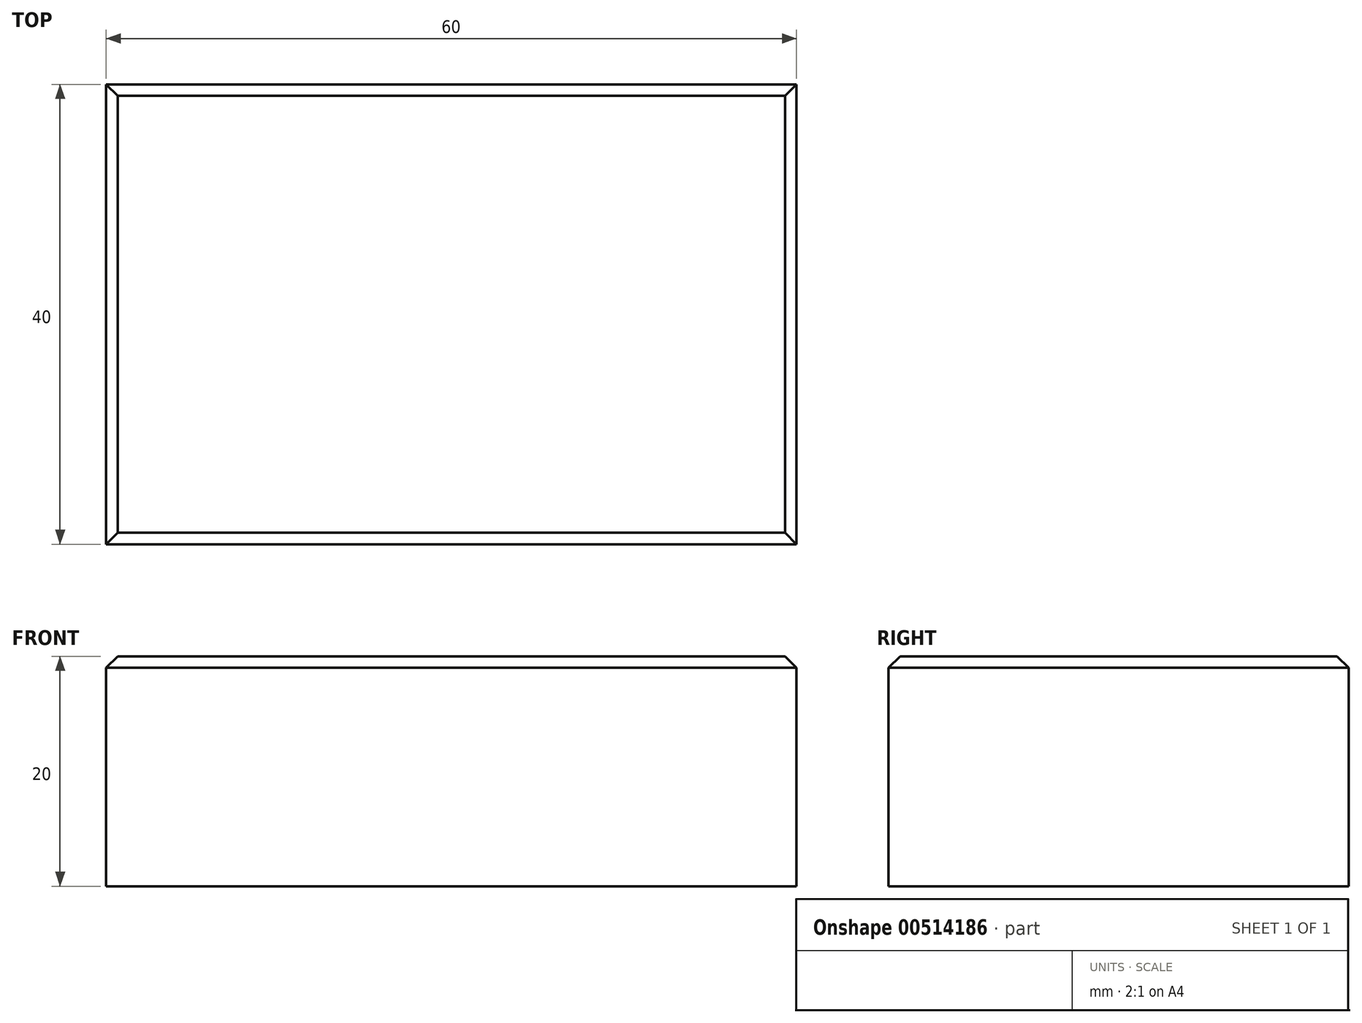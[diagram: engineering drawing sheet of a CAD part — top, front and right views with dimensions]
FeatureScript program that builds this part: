
annotation { "Feature Type Name" : "Feature", "Feature Type Description" : "" }
export const myFeature = defineFeature(function(context is Context, id is Id, definition is map)
    precondition{}
    {
        {
            var Q0;
            Q0=qCreatedBy(makeId("Top.planeOp"),FACE);
            var sketch = newSketch(context, id + "F0", { "sketchPlane" : qUnion([Q0])});
            skLineSegment(sketch, "E0.bottom", {"start": v(0, 0) * mm, "end": v(60, 0) * mm});
            skLineSegment(sketch, "E0.top", {"start": v(0, 40) * mm, "end": v(60, 40) * mm});
            skLineSegment(sketch, "E0.left", {"start": v(0, 0) * mm, "end": v(0, 40) * mm});
            skLineSegment(sketch, "E0.right", {"start": v(60, 0) * mm, "end": v(60, 40) * mm});
            skSolve(sketch);
        }
        {
            var Q0;
            Q0=qSketchRegion(id+"F0",true);
            extrude(context, id + "F1", {"entities" : qUnion([Q0]), "depth" : 20 * mm});
        }
        {
            var Q0;
            Q0=makeQuery(id+"F1.opExtrude","CAP_FACE",FACE,{"disambiguationData":[OSD([sQuery(id+"F0.wireOp",EDGE,"E0.bottom"),sQuery(id+"F0.wireOp",EDGE,"E0.top"),sQuery(id+"F0.wireOp",EDGE,"E0.left"),sQuery(id+"F0.wireOp",EDGE,"E0.right")])],"isStart":false});
            chamfer(context, id + "F2", {"entities" : qUnion([Q0]), "width" : 1 * mm, "tangentPropagation" : true});
        }
    });
